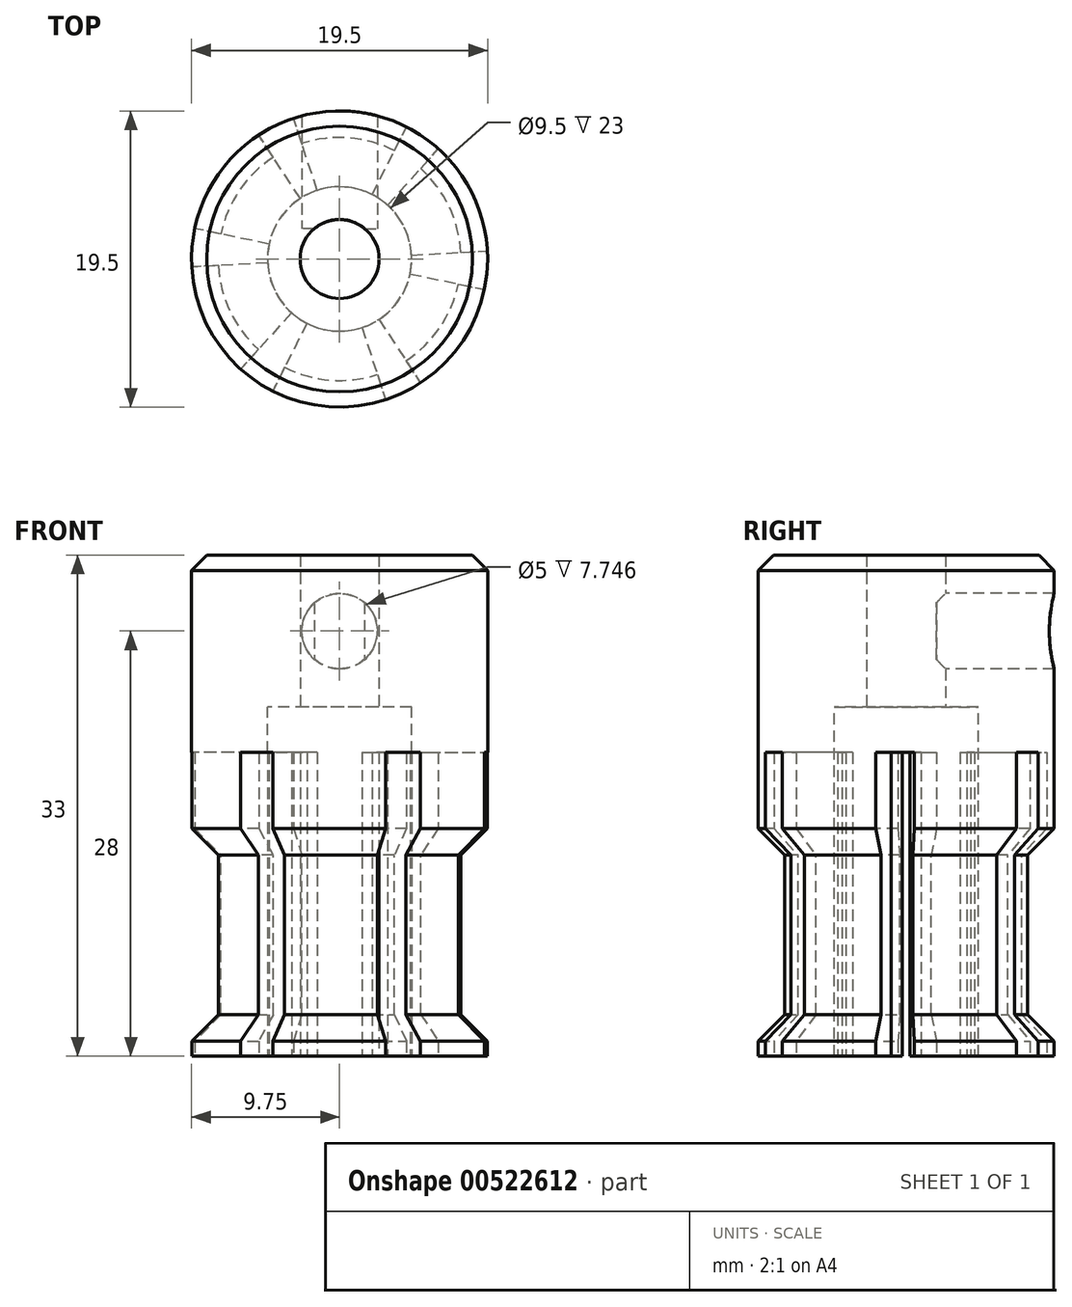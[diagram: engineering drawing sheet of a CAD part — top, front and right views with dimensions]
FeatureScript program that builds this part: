
annotation { "Feature Type Name" : "Feature", "Feature Type Description" : "" }
export const myFeature = defineFeature(function(context is Context, id is Id, definition is map)
    precondition{}
    {
        {
            var Q0;
            Q0=qCreatedBy(makeId("Top.planeOp"),FACE);
            var sketch = newSketch(context, id + "F0", { "sketchPlane" : qUnion([Q0])});
            skCircle(sketch, "E0", {"center": v(0, -2) * mm, "radius": 4.75 * mm});
            skCircle(sketch, "E1", {"center": v(0, -2) * mm, "radius": 9.75 * mm});
            skCircle(sketch, "E2", {"center": v(0, -2) * mm, "radius": 2.6 * mm});
            skSolve(sketch);
        }
        {
            var Q0;
            Q0=makeQuery(id+"F0.imprint","IMPRINT",FACE,{"disambiguationData":[TD([[makeQuery(id+"F0.imprint","IMPRINT",EDGE,{"derivedFrom":sQuery(id+"F0.wireOp",EDGE,"E0")}),-1.0]])]});
            var Q1;
            Q1=makeQuery(id+"F0.imprint","IMPRINT",FACE,{"disambiguationData":[TD([[makeQuery(id+"F0.imprint","IMPRINT",EDGE,{"derivedFrom":sQuery(id+"F0.wireOp",EDGE,"E0")}),1.0]])]});
            extrude(context, id + "F1", {"entities" : qUnion([Q0, Q1]), "depth" : 10 * mm});
        }
        {
            var Q0;
            Q0=makeQuery(id+"F0.imprint","IMPRINT",FACE,{"disambiguationData":[TD([[makeQuery(id+"F0.imprint","IMPRINT",EDGE,{"derivedFrom":sQuery(id+"F0.wireOp",EDGE,"E0")}),-1.0]])]});
            extrude(context, id + "F2", {"entities" : qUnion([Q0]), "operationType" : NewBodyOperationType.ADD, "oppositeDirection" : true, "depth" : 10 * mm});
        }
        {
            var Q0;
            Q0=makeQuery(id+"F2.opExtrude","CAP_FACE",FACE,{"disambiguationData":[OSD([sQuery(id+"F0.wireOp",EDGE,"E0"),sQuery(id+"F0.wireOp",EDGE,"E1")])],"isStart":false});
            var sketch = newSketch(context, id + "F3", { "sketchPlane" : qUnion([Q0])});
            skCircle(sketch, "E3", {"center": v(0, 2) * mm, "radius": 8 * mm});
            skSolve(sketch);
        }
        {
            var Q0;
            Q0=makeQuery(id+"F3.imprint","IMPRINT",FACE,{"disambiguationData":[TD([[makeQuery(id+"F3.imprint","IMPRINT",EDGE,{"derivedFrom":sQuery(id+"F3.wireOp",EDGE,"E3")}),1.0]])]});
            extrude(context, id + "F4", {"entities" : qUnion([Q0]), "operationType" : NewBodyOperationType.ADD, "depth" : 10 * mm});
        }
        {
            var Q0;
            Q0=makeQuery(id+"F4.opExtrude","CAP_FACE",FACE,{"disambiguationData":[OSD([sQuery(id+"F0.wireOp",EDGE,"E0"),sQuery(id+"F3.wireOp",EDGE,"E3")])],"isStart":false});
            var sketch = newSketch(context, id + "F5", { "sketchPlane" : qUnion([Q0])});
            skCircle(sketch, "E4", {"center": v(0, 2) * mm, "radius": 9.75 * mm});
            skSolve(sketch);
        }
        {
            var Q0;
            Q0=makeQuery(id+"F5.imprint","IMPRINT",FACE,{"disambiguationData":[TD([[makeQuery(id+"F5.imprint","IMPRINT",EDGE,{"derivedFrom":makeQuery(id+"F4.opExtrude","CAP_EDGE",EDGE,{"disambiguationData":[OSD([sQuery(id+"F3.wireOp",EDGE,"E3")])],"isStart":false})}),1.0]])]});
            var Q1;
            Q1=makeQuery(id+"F5.imprint","IMPRINT",FACE,{"disambiguationData":[TD([[makeQuery(id+"F5.imprint","IMPRINT",EDGE,{"derivedFrom":sQuery(id+"F5.wireOp",EDGE,"E4")}),1.0]])]});
            extrude(context, id + "F6", {"entities" : qUnion([Q0, Q1]), "operationType" : NewBodyOperationType.ADD, "depth" : 3 * mm});
        }
        {
            var Q0;
            Q0=makeQuery(id+"F6.opExtrude","CAP_EDGE",EDGE,{"disambiguationData":[OSD([sQuery(id+"F5.wireOp",EDGE,"E4")])],"isStart":true});
            chamfer(context, id + "F7", {"entities" : qUnion([Q0]), "width" : 2 * mm, "tangentPropagation" : true});
        }
        {
            var Q0;
            Q0=makeQuery(id+"F6.opExtrude","CAP_FACE",FACE,{"disambiguationData":[OSD([sQuery(id+"F0.wireOp",EDGE,"E0"),sQuery(id+"F5.wireOp",EDGE,"E4")])],"isStart":false});
            var sketch = newSketch(context, id + "F8", { "sketchPlane" : qUnion([Q0])});
            skLineSegment(sketch, "E5", {"start": v(0, 2) * mm, "end": v(-9.54, 0) * mm});
            skLineSegment(sketch, "E6", {"start": v(0, 2) * mm, "end": v(-5.33, -6.16) * mm});
            skLineSegment(sketch, "E7.1.0", {"start": v(0, 2) * mm, "end": v(-6.5, 9.27) * mm});
            skLineSegment(sketch, "E7.1.1", {"start": v(0, 2) * mm, "end": v(-9.74, 2.54) * mm});
            skLineSegment(sketch, "E7.2.0", {"start": v(0, 2) * mm, "end": v(3.03, 11.27) * mm});
            skLineSegment(sketch, "E7.2.1", {"start": v(0, 2) * mm, "end": v(-4.4, 10.7) * mm});
            skLineSegment(sketch, "E7.3.0", {"start": v(0, 2) * mm, "end": v(9.54, 4.01) * mm});
            skLineSegment(sketch, "E7.3.1", {"start": v(0, 2) * mm, "end": v(5.33, 10.17) * mm});
            skLineSegment(sketch, "E7.4.0", {"start": v(0, 2) * mm, "end": v(6.5, -5.25) * mm});
            skLineSegment(sketch, "E7.4.1", {"start": v(0, 2) * mm, "end": v(9.74, 1.48) * mm});
            skLineSegment(sketch, "E7.5.0", {"start": v(0, 2) * mm, "end": v(-3.03, -7.26) * mm});
            skLineSegment(sketch, "E7.5.1", {"start": v(0, 2) * mm, "end": v(4.4, -6.69) * mm});
            skPoint(sketch, "E7.center", {"position": v(0, 2) * mm});
            skLineSegment(sketch, "E7.anchor1", {"start": v(0, 2) * mm, "end": v(-9.54, 0) * mm, "construction": true});
            skLineSegment(sketch, "E7.anchor2", {"start": v(0, 2) * mm, "end": v(-3.03, -7.26) * mm, "construction": true});
            skSolve(sketch);
        }
        {
            var Q0;
            {var subQ0=sQuery(id+"F8.wireOp",EDGE,"E6");var subQ1=makeQuery(id+"F6.opExtrude","CAP_EDGE",EDGE,{"disambiguationData":[OSD([sQuery(id+"F5.wireOp",EDGE,"E4")])],"isStart":false});var subQ2=makeQuery(id+"F8.imprint","INTERSECT",VERTEX,{"derivedFrom":[subQ1,subQ0]});Q0=makeQuery(id+"F8.imprint","IMPRINT",FACE,{"disambiguationData":[TD([[makeQuery(id+"F8.imprint","IMPRINT",EDGE,{"disambiguationData":[TD([[subQ2,1.0]])],"derivedFrom":subQ0}),1.0]])]});}
            var Q1;
            {var subQ0=sQuery(id+"F8.wireOp",EDGE,"E7.4.0");var subQ1=makeQuery(id+"F6.opExtrude","CAP_EDGE",EDGE,{"disambiguationData":[OSD([sQuery(id+"F5.wireOp",EDGE,"E4")])],"isStart":false});var subQ2=makeQuery(id+"F8.imprint","INTERSECT",VERTEX,{"derivedFrom":[subQ1,subQ0]});Q1=makeQuery(id+"F8.imprint","IMPRINT",FACE,{"disambiguationData":[TD([[makeQuery(id+"F8.imprint","IMPRINT",EDGE,{"disambiguationData":[TD([[subQ2,1.0]])],"derivedFrom":subQ0}),-1.0]])]});}
            var Q2;
            {var subQ0=sQuery(id+"F8.wireOp",EDGE,"E7.3.0");var subQ1=makeQuery(id+"F6.opExtrude","CAP_EDGE",EDGE,{"disambiguationData":[OSD([sQuery(id+"F5.wireOp",EDGE,"E4")])],"isStart":false});var subQ2=makeQuery(id+"F8.imprint","INTERSECT",VERTEX,{"derivedFrom":[subQ1,subQ0]});Q2=makeQuery(id+"F8.imprint","IMPRINT",FACE,{"disambiguationData":[TD([[makeQuery(id+"F8.imprint","IMPRINT",EDGE,{"disambiguationData":[TD([[subQ2,1.0]])],"derivedFrom":subQ0}),-1.0]])]});}
            var Q3;
            {var subQ0=sQuery(id+"F8.wireOp",EDGE,"E7.2.0");var subQ1=makeQuery(id+"F6.opExtrude","CAP_EDGE",EDGE,{"disambiguationData":[OSD([sQuery(id+"F5.wireOp",EDGE,"E4")])],"isStart":false});var subQ2=makeQuery(id+"F8.imprint","INTERSECT",VERTEX,{"derivedFrom":[subQ1,subQ0]});Q3=makeQuery(id+"F8.imprint","IMPRINT",FACE,{"disambiguationData":[TD([[makeQuery(id+"F8.imprint","IMPRINT",EDGE,{"disambiguationData":[TD([[subQ2,1.0]])],"derivedFrom":subQ0}),-1.0]])]});}
            var Q4;
            {var subQ0=sQuery(id+"F8.wireOp",EDGE,"E7.1.0");var subQ1=makeQuery(id+"F6.opExtrude","CAP_EDGE",EDGE,{"disambiguationData":[OSD([sQuery(id+"F5.wireOp",EDGE,"E4")])],"isStart":false});var subQ2=makeQuery(id+"F8.imprint","INTERSECT",VERTEX,{"derivedFrom":[subQ1,subQ0]});Q4=makeQuery(id+"F8.imprint","IMPRINT",FACE,{"disambiguationData":[TD([[makeQuery(id+"F8.imprint","IMPRINT",EDGE,{"disambiguationData":[TD([[subQ2,1.0]])],"derivedFrom":subQ0}),-1.0]])]});}
            var Q5;
            {var subQ0=sQuery(id+"F8.wireOp",EDGE,"E5");var subQ1=makeQuery(id+"F6.opExtrude","CAP_EDGE",EDGE,{"disambiguationData":[OSD([sQuery(id+"F5.wireOp",EDGE,"E4")])],"isStart":false});var subQ2=makeQuery(id+"F8.imprint","INTERSECT",VERTEX,{"derivedFrom":[subQ1,subQ0]});Q5=makeQuery(id+"F8.imprint","IMPRINT",FACE,{"disambiguationData":[TD([[makeQuery(id+"F8.imprint","IMPRINT",EDGE,{"disambiguationData":[TD([[subQ2,1.0]])],"derivedFrom":subQ0}),-1.0]])]});}
            extrude(context, id + "F9", {"entities" : qUnion([Q0, Q1, Q2, Q3, Q4, Q5]), "operationType" : NewBodyOperationType.REMOVE, "oppositeDirection" : true, "depth" : 20 * mm});
        }
        {
            var Q0;
            Q0=qCreatedBy(makeId("Front.planeOp"),FACE);
            var sketch = newSketch(context, id + "F10", { "sketchPlane" : qUnion([Q0])});
            skPoint(sketch, "E8", {"position": v(0, 5) * mm});
            skSolve(sketch);
        }
        {
            var Q0;
            Q0=sQuery(id+"F10.wireOp",VERTEX,"E8");
            var Q1;
            Q1=makeQuery(id+"F1.opExtrude","SWEPT_BODY",BODY,{"disambiguationData":[OSD([sQuery(id+"F0.wireOp",EDGE,"E1"),sQuery(id+"F0.wireOp",EDGE,"E2")])]});
            hole(context, id + "F11", {"style" : HoleStyle.SIMPLE, "endStyle" : HoleEndStyle.BLIND, "holeDiameter" : 5 * mm, "holeDepth" : 14 * mm, "locations" : qUnion([Q0]), "scope" : qUnion([Q1])});
        }
        {
            var Q0;
            Q0=makeQuery(id+"F1.opExtrude","CAP_EDGE",EDGE,{"disambiguationData":[OSD([sQuery(id+"F0.wireOp",EDGE,"E1")])],"isStart":false});
            chamfer(context, id + "F12", {"entities" : qUnion([Q0]), "width" : 1 * mm, "tangentPropagation" : true});
        }
        {
            var Q0;
            {var subQ0=sQuery(id+"F0.wireOp",EDGE,"E1");Q0=makeQuery(id+"F9.boolean.opBoolean","SPLIT",EDGE,{"disambiguationData":[TD([makeQuery(id+"F9.opExtrude","SWEPT_FACE",FACE,{"disambiguationData":[OSD([sQuery(id+"F8.wireOp",EDGE,"E7.5.0")])]})])],"derivedFrom":makeQuery(id+"F2.opExtrude","CAP_EDGE",EDGE,{"disambiguationData":[OSD([subQ0])],"isStart":false})});}
            var Q1;
            {var subQ0=sQuery(id+"F0.wireOp",EDGE,"E1");Q1=makeQuery(id+"F9.boolean.opBoolean","SPLIT",EDGE,{"disambiguationData":[TD([makeQuery(id+"F9.opExtrude","SWEPT_FACE",FACE,{"disambiguationData":[OSD([sQuery(id+"F8.wireOp",EDGE,"E5")])]})])],"derivedFrom":makeQuery(id+"F2.opExtrude","CAP_EDGE",EDGE,{"disambiguationData":[OSD([subQ0])],"isStart":false})});}
            var Q2;
            {var subQ0=sQuery(id+"F0.wireOp",EDGE,"E1");Q2=makeQuery(id+"F9.boolean.opBoolean","SPLIT",EDGE,{"disambiguationData":[TD([makeQuery(id+"F9.opExtrude","SWEPT_FACE",FACE,{"disambiguationData":[OSD([sQuery(id+"F8.wireOp",EDGE,"E7.4.0")])]})])],"derivedFrom":makeQuery(id+"F2.opExtrude","CAP_EDGE",EDGE,{"disambiguationData":[OSD([subQ0])],"isStart":false})});}
            var Q3;
            {var subQ0=sQuery(id+"F0.wireOp",EDGE,"E1");Q3=makeQuery(id+"F9.boolean.opBoolean","SPLIT",EDGE,{"disambiguationData":[TD([makeQuery(id+"F9.opExtrude","SWEPT_FACE",FACE,{"disambiguationData":[OSD([sQuery(id+"F8.wireOp",EDGE,"E7.3.0")])]})])],"derivedFrom":makeQuery(id+"F2.opExtrude","CAP_EDGE",EDGE,{"disambiguationData":[OSD([subQ0])],"isStart":false})});}
            var Q4;
            {var subQ0=sQuery(id+"F0.wireOp",EDGE,"E1");Q4=makeQuery(id+"F9.boolean.opBoolean","SPLIT",EDGE,{"disambiguationData":[TD([makeQuery(id+"F9.opExtrude","SWEPT_FACE",FACE,{"disambiguationData":[OSD([sQuery(id+"F8.wireOp",EDGE,"E7.2.0")])]})])],"derivedFrom":makeQuery(id+"F2.opExtrude","CAP_EDGE",EDGE,{"disambiguationData":[OSD([subQ0])],"isStart":false})});}
            var Q5;
            {var subQ0=sQuery(id+"F0.wireOp",EDGE,"E1");Q5=makeQuery(id+"F9.boolean.opBoolean","SPLIT",EDGE,{"disambiguationData":[TD([makeQuery(id+"F9.opExtrude","SWEPT_FACE",FACE,{"disambiguationData":[OSD([sQuery(id+"F8.wireOp",EDGE,"E7.1.0")])]})])],"derivedFrom":makeQuery(id+"F2.opExtrude","CAP_EDGE",EDGE,{"disambiguationData":[OSD([subQ0])],"isStart":false})});}
            chamfer(context, id + "F13", {"entities" : qUnion([Q0, Q1, Q2, Q3, Q4, Q5]), "width" : 2 * mm, "tangentPropagation" : true});
        }
    });
